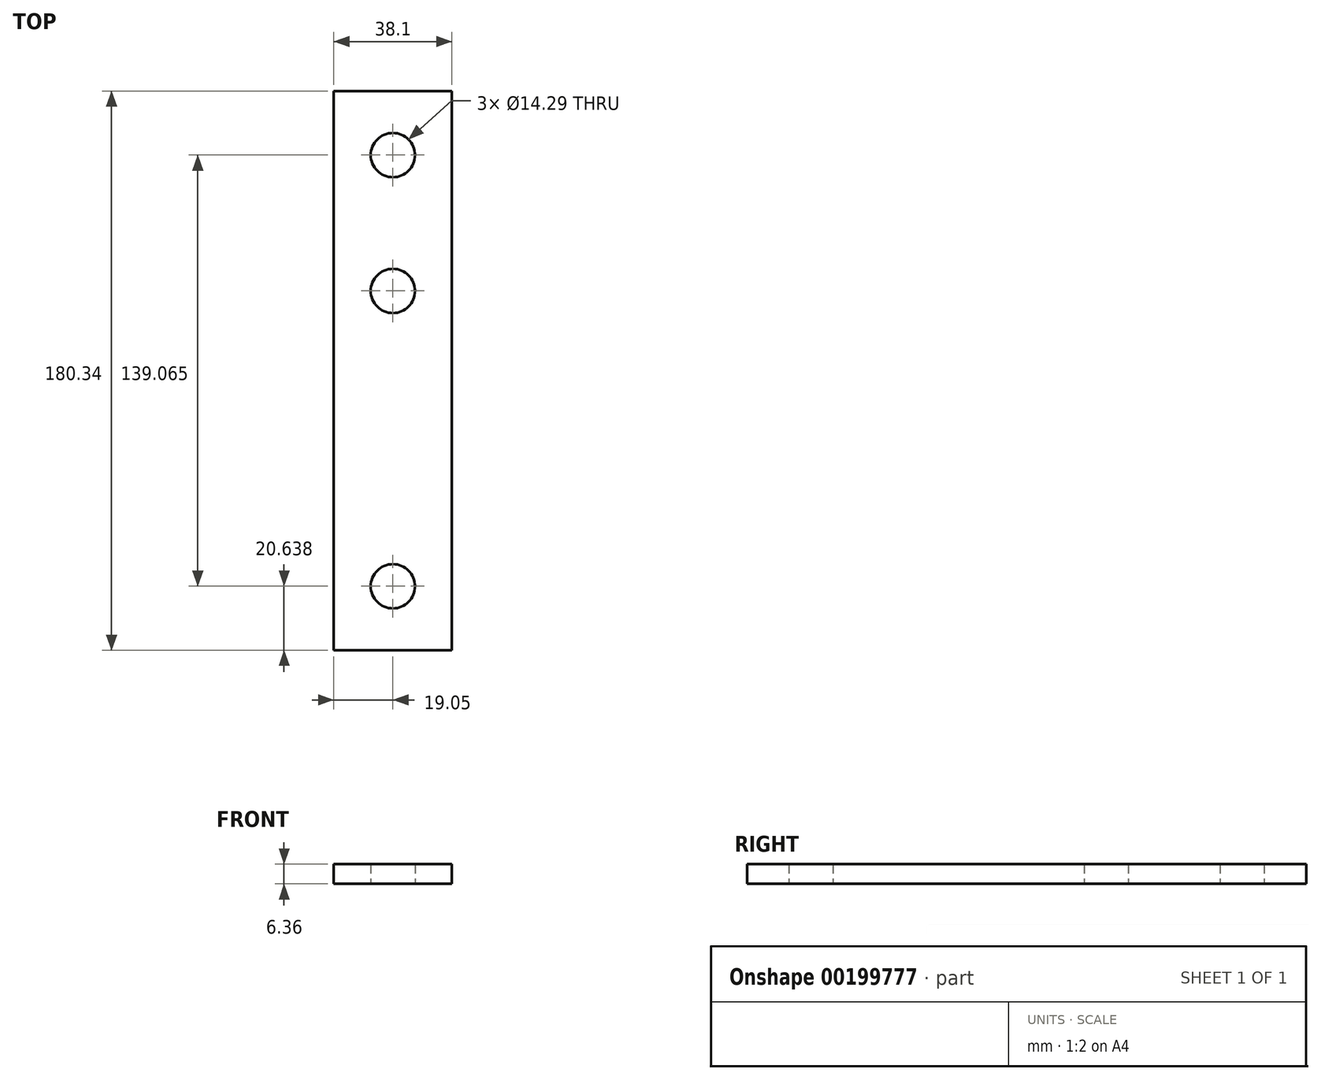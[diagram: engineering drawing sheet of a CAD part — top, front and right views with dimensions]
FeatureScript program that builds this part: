
annotation { "Feature Type Name" : "Feature", "Feature Type Description" : "" }
export const myFeature = defineFeature(function(context is Context, id is Id, definition is map)
    precondition{}
    {
        {
            var Q0;
            Q0=qCreatedBy(makeId("Top.planeOp"),FACE);
            var sketch = newSketch(context, id + "F0", { "sketchPlane" : qUnion([Q0])});
            skLineSegment(sketch, "E0.0.0", {"start": v(19.05, -90.17) * mm, "end": v(19.05, 90.17) * mm});
            skLineSegment(sketch, "E0.0.1", {"start": v(19.05, 90.17) * mm, "end": v(-19.05, 90.17) * mm});
            skLineSegment(sketch, "E0.0.2", {"start": v(-19.05, 90.17) * mm, "end": v(-19.05, -90.17) * mm});
            skLineSegment(sketch, "E0.0.3", {"start": v(-19.05, -90.17) * mm, "end": v(19.05, -90.17) * mm});
            skCircle(sketch, "E1.0", {"center": v(0, 69.53) * mm, "radius": 7.14 * mm});
            skCircle(sketch, "E1.1", {"center": v(0, 25.72) * mm, "radius": 7.14 * mm});
            skCircle(sketch, "E1.2", {"center": v(0, -69.53) * mm, "radius": 7.14 * mm});
            skSolve(sketch);
        }
        {
            var Q0;
            Q0 = qSketchRegion(id + "F0", true);
            extrude(context, id + "F1", {"entities" : qUnion([Q0]), "endBound" : BoundingType.SYMMETRIC, "depth" : 6.35 * mm});
        }
    });
